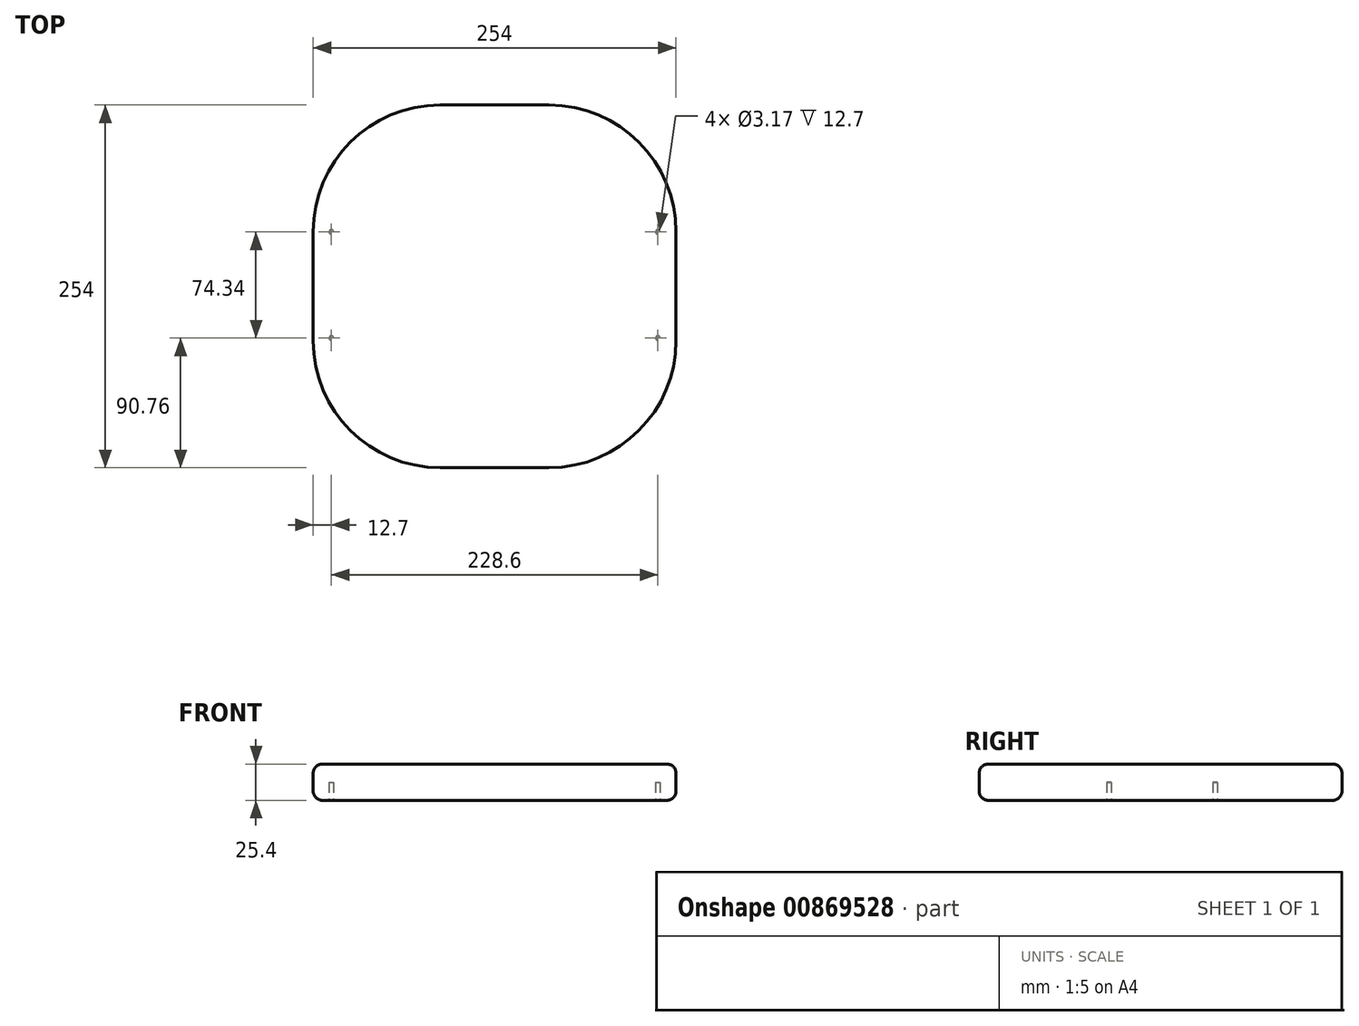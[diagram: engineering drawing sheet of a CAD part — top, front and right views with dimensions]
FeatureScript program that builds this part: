
annotation { "Feature Type Name" : "Feature", "Feature Type Description" : "" }
export const myFeature = defineFeature(function(context is Context, id is Id, definition is map)
    precondition{}
    {
        {
            var Q0;
            Q0=qCreatedBy(makeId("Top.planeOp"),FACE);
            var sketch = newSketch(context, id + "F0", { "sketchPlane" : qUnion([Q0])});
            skLineSegment(sketch, "E0.bottom", {"start": v(38.1, 127) * mm, "end": v(-38.1, 127) * mm});
            skLineSegment(sketch, "E0.top", {"start": v(38.1, -127) * mm, "end": v(-38.1, -127) * mm});
            skLineSegment(sketch, "E0.left", {"start": v(127, 38.1) * mm, "end": v(127, -38.1) * mm});
            skLineSegment(sketch, "E0.right", {"start": v(-127, 38.1) * mm, "end": v(-127, -38.1) * mm});
            skPoint(sketch, "E0.middle", {"position": v(0, 0) * mm});
            skPoint(sketch, "E1.visualSharp", {"position": v(-127, 127) * mm});
            skArc(sketch, "E1.filletArc", {"start": v(-38.1, 127) * mm, "mid": v(-100.96, 100.96) * mm, "end": v(-127, 38.1) * mm});
            skPoint(sketch, "E2.visualSharp", {"position": v(127, 127) * mm});
            skArc(sketch, "E2.filletArc", {"start": v(127, 38.1) * mm, "mid": v(100.96, 100.96) * mm, "end": v(38.1, 127) * mm});
            skPoint(sketch, "E3.visualSharp", {"position": v(-127, -127) * mm});
            skArc(sketch, "E3.filletArc", {"start": v(-127, -38.1) * mm, "mid": v(-100.96, -100.96) * mm, "end": v(-38.1, -127) * mm});
            skPoint(sketch, "E4.visualSharp", {"position": v(127, -127) * mm});
            skArc(sketch, "E4.filletArc", {"start": v(38.1, -127) * mm, "mid": v(100.96, -100.96) * mm, "end": v(127, -38.1) * mm});
            skSolve(sketch);
        }
        {
            var Q0;
            Q0 = qSketchRegion(id + "F0", true);
            extrude(context, id + "F1", {"entities" : qUnion([Q0]), "depth" : 25.4 * mm, "offsetDistance" : 25.4 * mm});
        }
        {
            var Q0;
            Q0=makeQuery(id+"F1.opExtrude","CAP_EDGE",EDGE,{"disambiguationData":[OSD([sQuery(id+"F0.wireOp",EDGE,"E3.filletArc")])],"isStart":false});
            var Q1;
            Q1=makeQuery(id+"F1.opExtrude","CAP_EDGE",EDGE,{"disambiguationData":[OSD([sQuery(id+"F0.wireOp",EDGE,"E3.filletArc")])],"isStart":true});
            fillet(context, id + "F2", {"entities" : qUnion([Q0, Q1]), "radius" : 6.35 * mm, "tangentPropagation" : true, "allowEdgeOverflow" : false});
        }
        {
            var Q0;
            Q0=makeQuery(id+"F1.opExtrude","CAP_FACE",FACE,{"disambiguationData":[OSD([sQuery(id+"F0.wireOp",EDGE,"E0.bottom"),sQuery(id+"F0.wireOp",EDGE,"E0.top"),sQuery(id+"F0.wireOp",EDGE,"E0.left"),sQuery(id+"F0.wireOp",EDGE,"E0.right"),sQuery(id+"F0.wireOp",EDGE,"E1.filletArc"),sQuery(id+"F0.wireOp",EDGE,"E2.filletArc"),sQuery(id+"F0.wireOp",EDGE,"E3.filletArc"),sQuery(id+"F0.wireOp",EDGE,"E4.filletArc")])],"isStart":true});
            var sketch = newSketch(context, id + "F3", { "sketchPlane" : qUnion([Q0])});
            skCircle(sketch, "E5", {"center": v(-114.3, 36.24) * mm, "radius": 1.59 * mm});
            skCircle(sketch, "E6", {"center": v(114.3, 36.24) * mm, "radius": 1.59 * mm});
            skCircle(sketch, "E7", {"center": v(114.3, -38.1) * mm, "radius": 1.59 * mm});
            skCircle(sketch, "E8", {"center": v(-114.3, -38.1) * mm, "radius": 1.59 * mm});
            skSolve(sketch);
        }
        {
            var Q0;
            Q0 = qSketchRegion(id + "F3", true);
            extrude(context, id + "F4", {"entities" : qUnion([Q0]), "operationType" : NewBodyOperationType.REMOVE, "oppositeDirection" : true, "depth" : 12.7 * mm, "offsetDistance" : 25.4 * mm});
        }
    });
